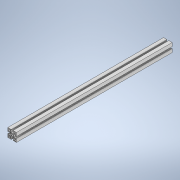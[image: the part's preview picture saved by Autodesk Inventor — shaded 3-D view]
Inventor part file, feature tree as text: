
AUTODESK INVENTOR PART (.ipt)
format: ipt  version: 2020 (Build 240168000, 168)  size: 202,240 bytes
history: native  units: mm
features: other x1, extrude x1, sketch x1
ambient origin geometry x8: Origin, YZ Plane, XZ Plane, XY Plane, X Axis, Y Axis, Z Axis, Center Point
bodies: Body1 (feature_tree)
feature tree (3):
  other  "솔리드1"
  extrude  "돌출1"  Depth=540.0mm TaperAngle=0.0deg
  sketch  "스케치1"
